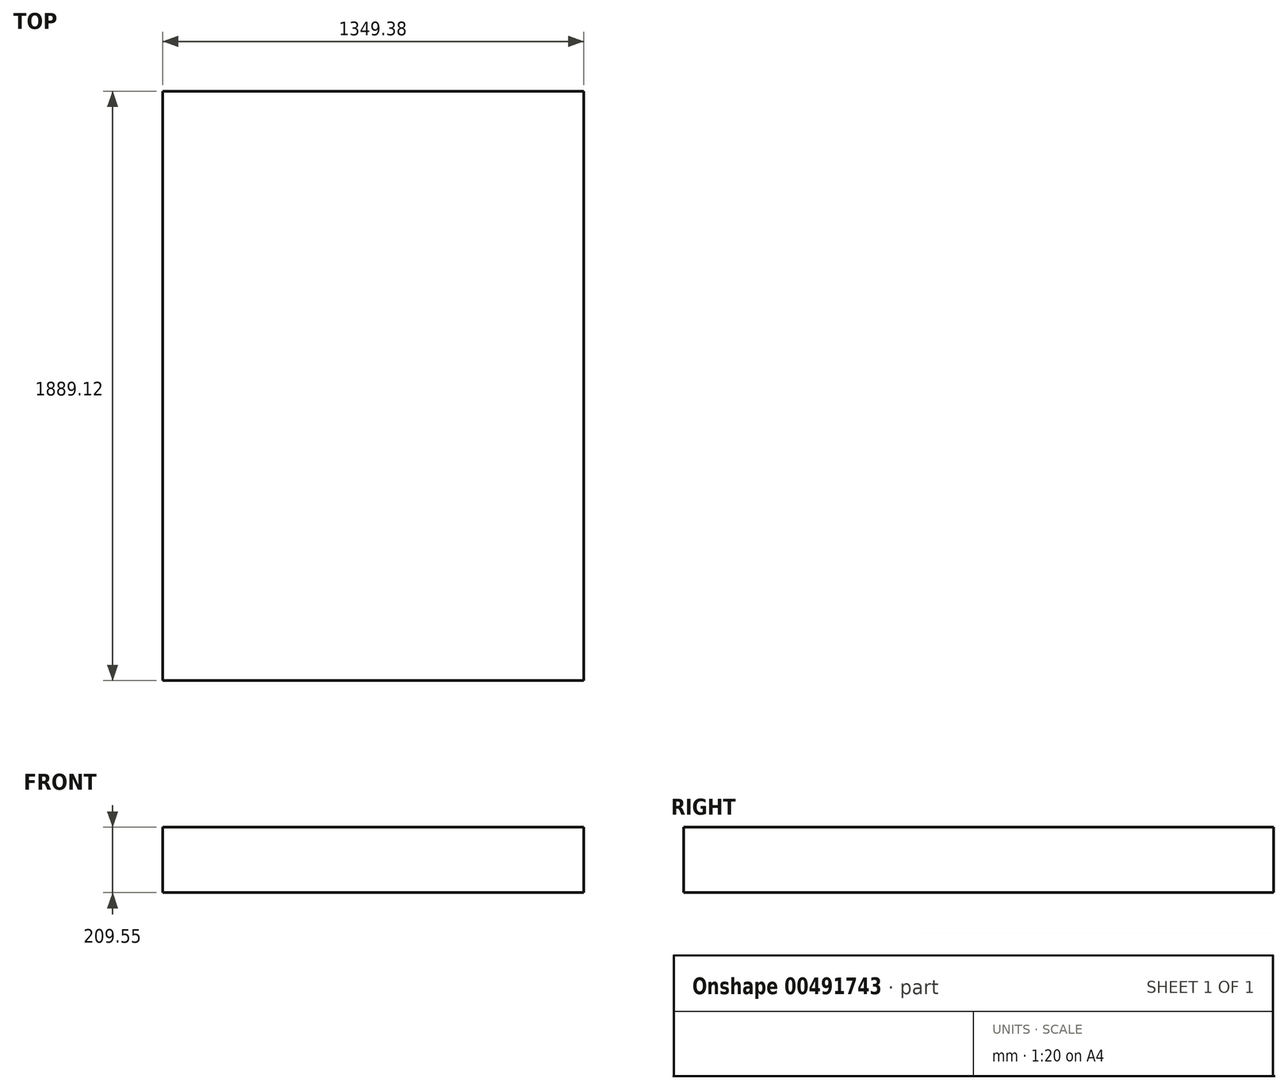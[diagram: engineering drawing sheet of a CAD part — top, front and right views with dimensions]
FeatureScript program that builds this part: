
annotation { "Feature Type Name" : "Feature", "Feature Type Description" : "" }
export const myFeature = defineFeature(function(context is Context, id is Id, definition is map)
    precondition{}
    {
        {
            var Q0;
            Q0=qCreatedBy(makeId("Top.planeOp"),FACE);
            var sketch = newSketch(context, id + "F0", { "sketchPlane" : qUnion([Q0])});
            skLineSegment(sketch, "E0.bottom", {"start": v(674.69, -944.56) * mm, "end": v(-674.69, -944.56) * mm});
            skLineSegment(sketch, "E0.top", {"start": v(674.69, 944.56) * mm, "end": v(-674.69, 944.56) * mm});
            skLineSegment(sketch, "E0.left", {"start": v(674.69, -944.56) * mm, "end": v(674.69, 944.56) * mm});
            skLineSegment(sketch, "E0.right", {"start": v(-674.69, -944.56) * mm, "end": v(-674.69, 944.56) * mm});
            skPoint(sketch, "E0.middle", {"position": v(0, 0) * mm});
            skSolve(sketch);
        }
        {
            var Q0;
            Q0 = qSketchRegion(id + "F0", true);
            extrude(context, id + "F1", {"entities" : qUnion([Q0]), "depth" : 209.55 * mm});
        }
    });
